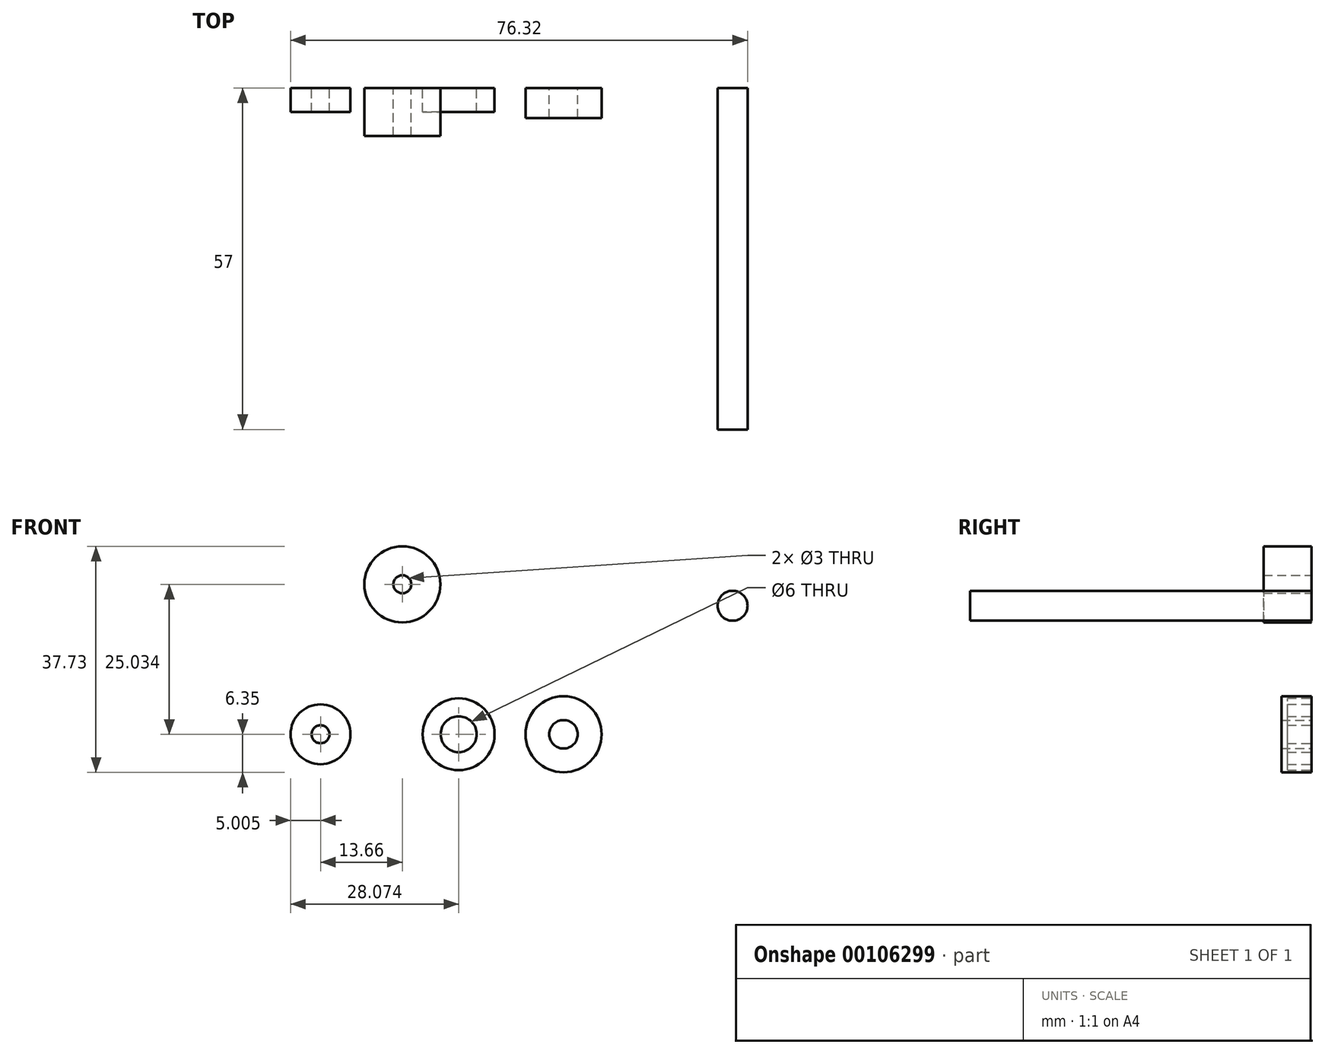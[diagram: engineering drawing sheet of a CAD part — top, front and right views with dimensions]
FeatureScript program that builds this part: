
annotation { "Feature Type Name" : "Feature", "Feature Type Description" : "" }
export const myFeature = defineFeature(function(context is Context, id is Id, definition is map)
    precondition{}
    {
        {
            var Q0;
            Q0=qCreatedBy(makeId("Front.planeOp"),FACE);
            var sketch = newSketch(context, id + "F0", { "sketchPlane" : qUnion([Q0])});
            skCircle(sketch, "E0", {"center": v(0, 0) * mm, "radius": 2.38 * mm});
            skCircle(sketch, "E1", {"center": v(0, 0) * mm, "radius": 6.35 * mm});
            skSolve(sketch);
        }
        {
            var Q0;
            Q0=qSketchRegion(id+"F0",true);
            extrude(context, id + "F1", {"entities" : qUnion([Q0]), "depth" : 5 * mm});
        }
        {
            var Q0;
            Q0=qCreatedBy(makeId("Front.planeOp"),FACE);
            var sketch = newSketch(context, id + "F2", { "sketchPlane" : qUnion([Q0])});
            skCircle(sketch, "E2", {"center": v(28.24, 21.45) * mm, "radius": 2.5 * mm});
            skSolve(sketch);
        }
        {
            var Q0;
            Q0=qSketchRegion(id+"F2",true);
            extrude(context, id + "F3", {"entities" : qUnion([Q0]), "depth" : 57 * mm});
        }
        {
            var Q0;
            Q0=qCreatedBy(makeId("Front.planeOp"),FACE);
            var sketch = newSketch(context, id + "F4", { "sketchPlane" : qUnion([Q0])});
            skCircle(sketch, "E3", {"center": v(-40.58, 0) * mm, "radius": 1.5 * mm});
            skCircle(sketch, "E4", {"center": v(-40.58, 0) * mm, "radius": 5 * mm});
            skSolve(sketch);
        }
        {
            var Q0;
            Q0=qSketchRegion(id+"F4",true);
            extrude(context, id + "F5", {"entities" : qUnion([Q0]), "depth" : 4 * mm});
        }
        {
            var Q0;
            Q0=qCreatedBy(makeId("Front.planeOp"),FACE);
            var sketch = newSketch(context, id + "F6", { "sketchPlane" : qUnion([Q0])});
            skCircle(sketch, "E5", {"center": v(-17.5, 0) * mm, "radius": 3 * mm});
            skCircle(sketch, "E6", {"center": v(-17.5, 0) * mm, "radius": 6 * mm});
            skSolve(sketch);
        }
        {
            var Q0;
            Q0 = qSketchRegion(id + "F6", true);
            extrude(context, id + "F7", {"entities" : qUnion([Q0]), "depth" : 4 * mm});
        }
        {
            var Q0;
            Q0=qCreatedBy(makeId("Front.planeOp"),FACE);
            var sketch = newSketch(context, id + "F8", { "sketchPlane" : qUnion([Q0])});
            skCircle(sketch, "E7", {"center": v(-26.92, 25.03) * mm, "radius": 6.35 * mm});
            skCircle(sketch, "E8", {"center": v(-26.92, 25.03) * mm, "radius": 1.5 * mm});
            skSolve(sketch);
        }
        {
            var Q0;
            Q0 = qSketchRegion(id + "F8", true);
            extrude(context, id + "F9", {"entities" : qUnion([Q0]), "depth" : 8 * mm});
        }
    });
